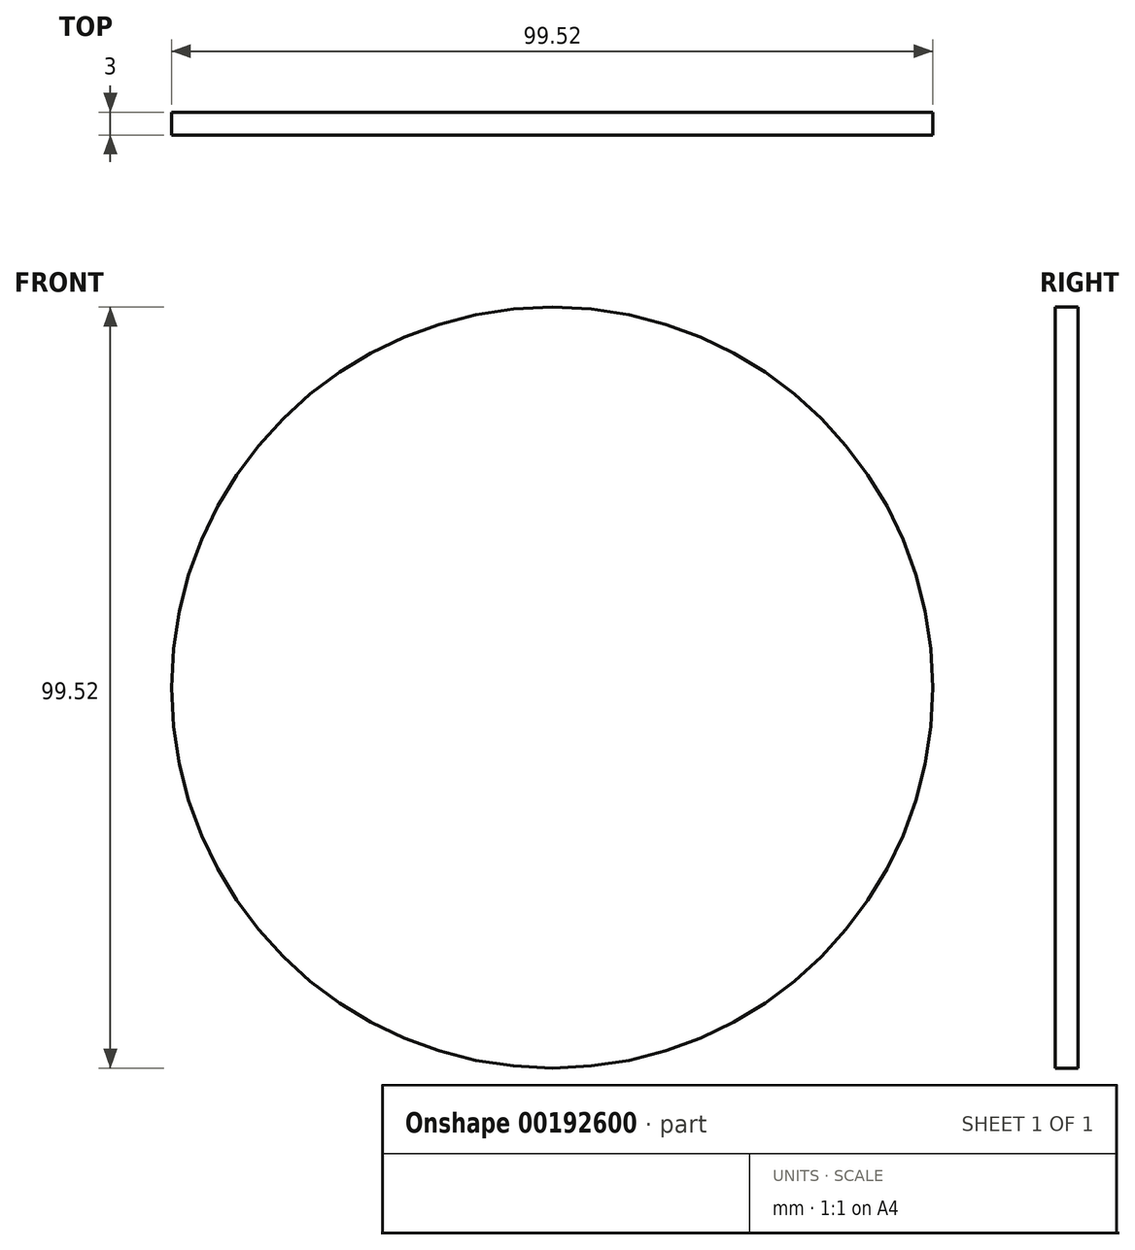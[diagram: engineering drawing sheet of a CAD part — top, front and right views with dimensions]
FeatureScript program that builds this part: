
annotation { "Feature Type Name" : "Feature", "Feature Type Description" : "" }
export const myFeature = defineFeature(function(context is Context, id is Id, definition is map)
    precondition{}
    {
        {
            var Q0;
            Q0=qCreatedBy(makeId("Front.planeOp"),FACE);
            var sketch = newSketch(context, id + "F0", { "sketchPlane" : qUnion([Q0])});
            skCircle(sketch, "E0", {"center": v(0, 0) * mm, "radius": 49.76 * mm});
            skSolve(sketch);
        }
        {
            var Q0;
            Q0=makeQuery(id+"F0.imprint","IMPRINT",FACE,{"disambiguationData":[TD([[makeQuery(id+"F0.imprint","IMPRINT",EDGE,{"derivedFrom":sQuery(id+"F0.wireOp",EDGE,"E0")}),1.0]])]});
            extrude(context, id + "F1", {"entities" : qUnion([Q0]), "depth" : 3 * mm});
        }
    });
